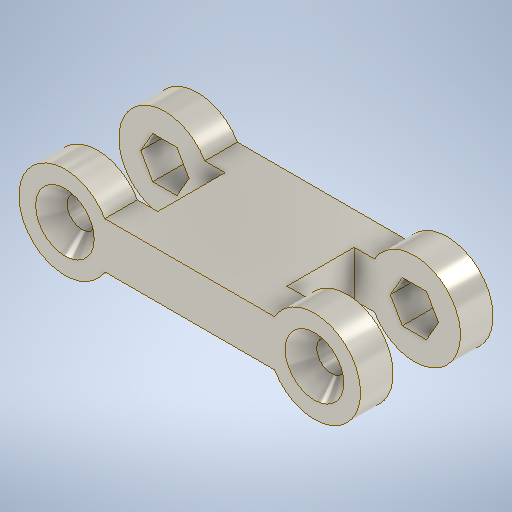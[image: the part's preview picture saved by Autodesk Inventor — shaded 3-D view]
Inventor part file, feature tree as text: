
AUTODESK INVENTOR PART (.ipt)
format: ipt  version: 2025.2 (Build 292293000, 293)  size: 317,952 bytes
history: native  units: mm
features: sketch x5, extrude x3, other x2, hole x2
ambient origin geometry x8: Origin, YZ Plane, XZ Plane, XY Plane, X Axis, Y Axis, Z Axis, Center Point
bodies: Body1 (feature_tree)
feature tree (12):
  other  "Barra1_0001_001"
  other  "Sólido1"
  extrude  "Extrusão1"  Depth=2.75mm
  extrude  "Extrusão2"  Depth=14.9075mm
  hole  "Furo1"  [1 undecoded]
  hole  "Furo2"  [1 undecoded]
  extrude  "Extrusão3"  Depth=15.430721mm
  sketch  "Esboço1"  dims[d5=2.75mm d6=2.75mm]
  sketch  "Esboço2"  dims[d7=11.0mm d9=14.9075mm]
  sketch  "Esboço3"  dims[d11=29.815mm d12=7.0mm]
  sketch  "Esboço4"  dims[d13=7.0mm d14=3.9mm d15=0.0mm]
  sketch  "Esboço5"  dims[d16=8.04mm d17=0.0mm d21=15.430721mm d23=3.5mm d24=6.0mm d25=7.0mm d26=2.0mm d27=14.3117mm d28=8.0mm d29=20.594885mm d30=3.5mm d31=6.0mm d32=7.0mm d33=2.0mm d34=14.3117mm d35=8.0mm d36=20.594885mm d37=11.0mm d38=3.0mm d39=3.0mm d40=3.9mm d41=0.0mm d22=0.5mm d42=0.0mm d43=0.0mm d44=0.0mm d45=0.0mm]
note: 2 required parameter values undecoded (feature->parameter linkage not recoverable at this tier; creation-order binding heuristic only, values carry confidence <= 0.55)
